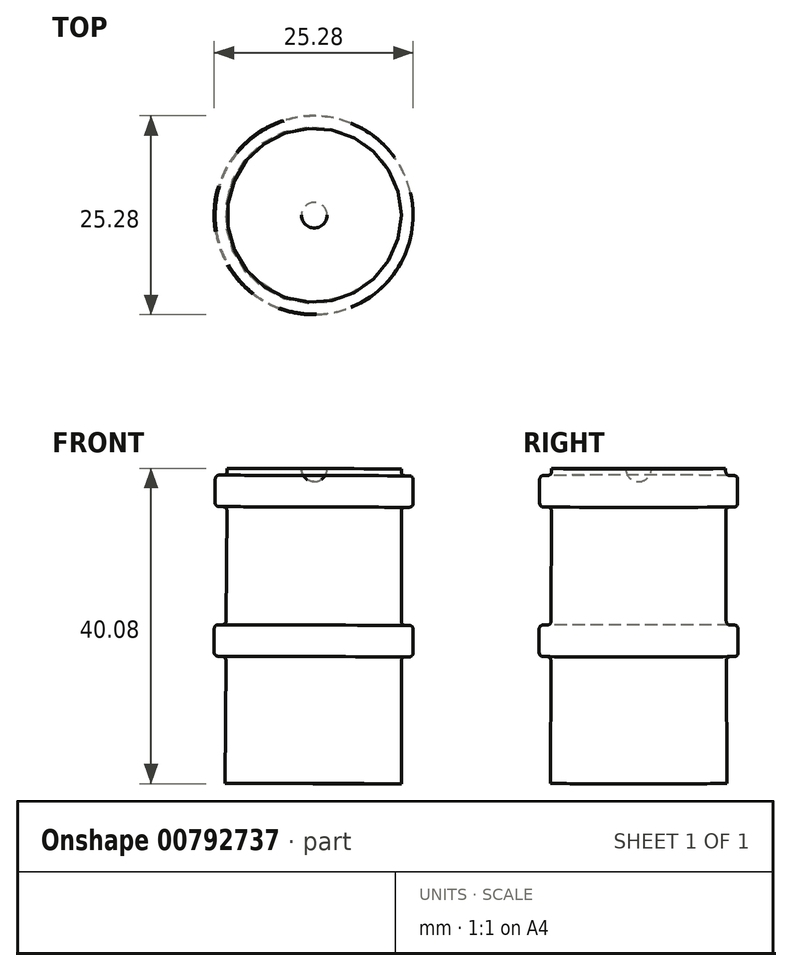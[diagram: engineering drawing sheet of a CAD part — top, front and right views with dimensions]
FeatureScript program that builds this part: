
annotation { "Feature Type Name" : "Feature", "Feature Type Description" : "" }
export const myFeature = defineFeature(function(context is Context, id is Id, definition is map)
    precondition{}
    {
        {
            var Q0;
            Q0=qCreatedBy(makeId("Front.planeOp"),FACE);
            var sketch = newSketch(context, id + "F0", { "sketchPlane" : qUnion([Q0])});
            skLineSegment(sketch, "E0.bottom", {"start": v(0.14, 17.38) * mm, "end": v(9.5, 17.38) * mm});
            skLineSegment(sketch, "E0.top", {"start": v(0.1, -20.12) * mm, "end": v(9.5, -20.12) * mm});
            skLineSegment(sketch, "E0.right", {"start": v(9.5, 17.38) * mm, "end": v(9.5, 9.86) * mm});
            skLineSegment(sketch, "E1", {"start": v(1.76, 19.88) * mm, "end": v(11.2, 19.88) * mm});
            skLineSegment(sketch, "E2", {"start": v(11.2, 19.88) * mm, "end": v(11.2, 19.5) * mm});
            skLineSegment(sketch, "E3", {"start": v(11.7, 19) * mm, "end": v(12.2, 19) * mm});
            skLineSegment(sketch, "E4", {"start": v(12.7, 18.5) * mm, "end": v(12.7, 15.5) * mm});
            skLineSegment(sketch, "E5", {"start": v(12.2, 15) * mm, "end": v(11.7, 15) * mm});
            skLineSegment(sketch, "E6", {"start": v(11.7, -4) * mm, "end": v(12.2, -4) * mm});
            skLineSegment(sketch, "E7", {"start": v(11.2, 14.5) * mm, "end": v(11.2, 0.5) * mm});
            skLineSegment(sketch, "E8", {"start": v(12.7, -0.5) * mm, "end": v(12.7, -3.5) * mm});
            skLineSegment(sketch, "E9", {"start": v(12.2, 0) * mm, "end": v(11.7, 0) * mm});
            skLineSegment(sketch, "E10", {"start": v(11.2, -4.5) * mm, "end": v(11.2, -20.12) * mm});
            skLineSegment(sketch, "E11", {"start": v(11.2, -20.12) * mm, "end": v(9.5, -20.12) * mm});
            skPoint(sketch, "E12.visualSharp", {"position": v(11.2, -4) * mm});
            skArc(sketch, "E12.filletArc", {"start": v(11.7, -4) * mm, "mid": v(11.35, -4.15) * mm, "end": v(11.2, -4.5) * mm});
            skPoint(sketch, "E13.visualSharp", {"position": v(11.2, 0) * mm});
            skArc(sketch, "E13.filletArc", {"start": v(11.2, 0.5) * mm, "mid": v(11.35, 0.15) * mm, "end": v(11.7, 0) * mm});
            skPoint(sketch, "E14.visualSharp", {"position": v(12.7, 0) * mm});
            skArc(sketch, "E14.filletArc", {"start": v(12.7, -0.5) * mm, "mid": v(12.55, -0.15) * mm, "end": v(12.2, 0) * mm});
            skPoint(sketch, "E15.visualSharp", {"position": v(12.7, -4) * mm});
            skArc(sketch, "E15.filletArc", {"start": v(12.2, -4) * mm, "mid": v(12.55, -3.85) * mm, "end": v(12.7, -3.5) * mm});
            skPoint(sketch, "E16.visualSharp", {"position": v(11.2, 19) * mm});
            skArc(sketch, "E16.filletArc", {"start": v(11.2, 19.5) * mm, "mid": v(11.35, 19.15) * mm, "end": v(11.7, 19) * mm});
            skPoint(sketch, "E17.visualSharp", {"position": v(11.2, 15) * mm});
            skArc(sketch, "E17.filletArc", {"start": v(11.7, 15) * mm, "mid": v(11.35, 14.85) * mm, "end": v(11.2, 14.5) * mm});
            skPoint(sketch, "E18.visualSharp", {"position": v(12.7, 19) * mm});
            skArc(sketch, "E18.filletArc", {"start": v(12.7, 18.5) * mm, "mid": v(12.55, 18.85) * mm, "end": v(12.2, 19) * mm});
            skPoint(sketch, "E19.visualSharp", {"position": v(12.7, 15) * mm});
            skArc(sketch, "E19.filletArc", {"start": v(12.2, 15) * mm, "mid": v(12.55, 15.15) * mm, "end": v(12.7, 15.5) * mm});
            skLineSegment(sketch, "E20", {"start": v(0, -20.12) * mm, "end": v(0.1, -20.12) * mm});
            skLineSegment(sketch, "E21", {"start": v(0.13, 18.25) * mm, "end": v(0, -20.12) * mm});
            skLineSegment(sketch, "E22", {"start": v(0.1, 9.86) * mm, "end": v(9.5, 9.86) * mm});
            skLineSegment(sketch, "E23", {"start": v(0.1, 9.9) * mm, "end": v(9.5, 9.86) * mm});
            skPoint(sketch, "E24", {"position": v(9.5, 9.2) * mm});
            skArc(sketch, "E25", {"start": v(9.5, 9.86) * mm, "mid": v(8.85, 9.2) * mm, "end": v(9.5, 8.56) * mm});
            skLineSegment(sketch, "E26", {"start": v(9.5, 8.56) * mm, "end": v(0, 8.6) * mm});
            skLineSegment(sketch, "E27.trimOffspring", {"start": v(9.5, 8.56) * mm, "end": v(9.5, -20.12) * mm});
            skArc(sketch, "E28", {"start": v(0.13, 18.25) * mm, "mid": v(1.29, 18.73) * mm, "end": v(1.76, 19.88) * mm});
            skSolve(sketch);
        }
        {
            var Q0;
            Q0 = qSketchRegion(id + "F0", true);
            var Q1;
            Q1=sQuery(id+"F0.wireOp",EDGE,"E21");
            revolve(context, id + "F1", {"surfaceOperationType" : NewSurfaceOperationType.NEW, "entities" : qUnion([Q0]), "axis" : qUnion([Q1]), "revolveType" : RevolveType.FULL});
        }
    });
